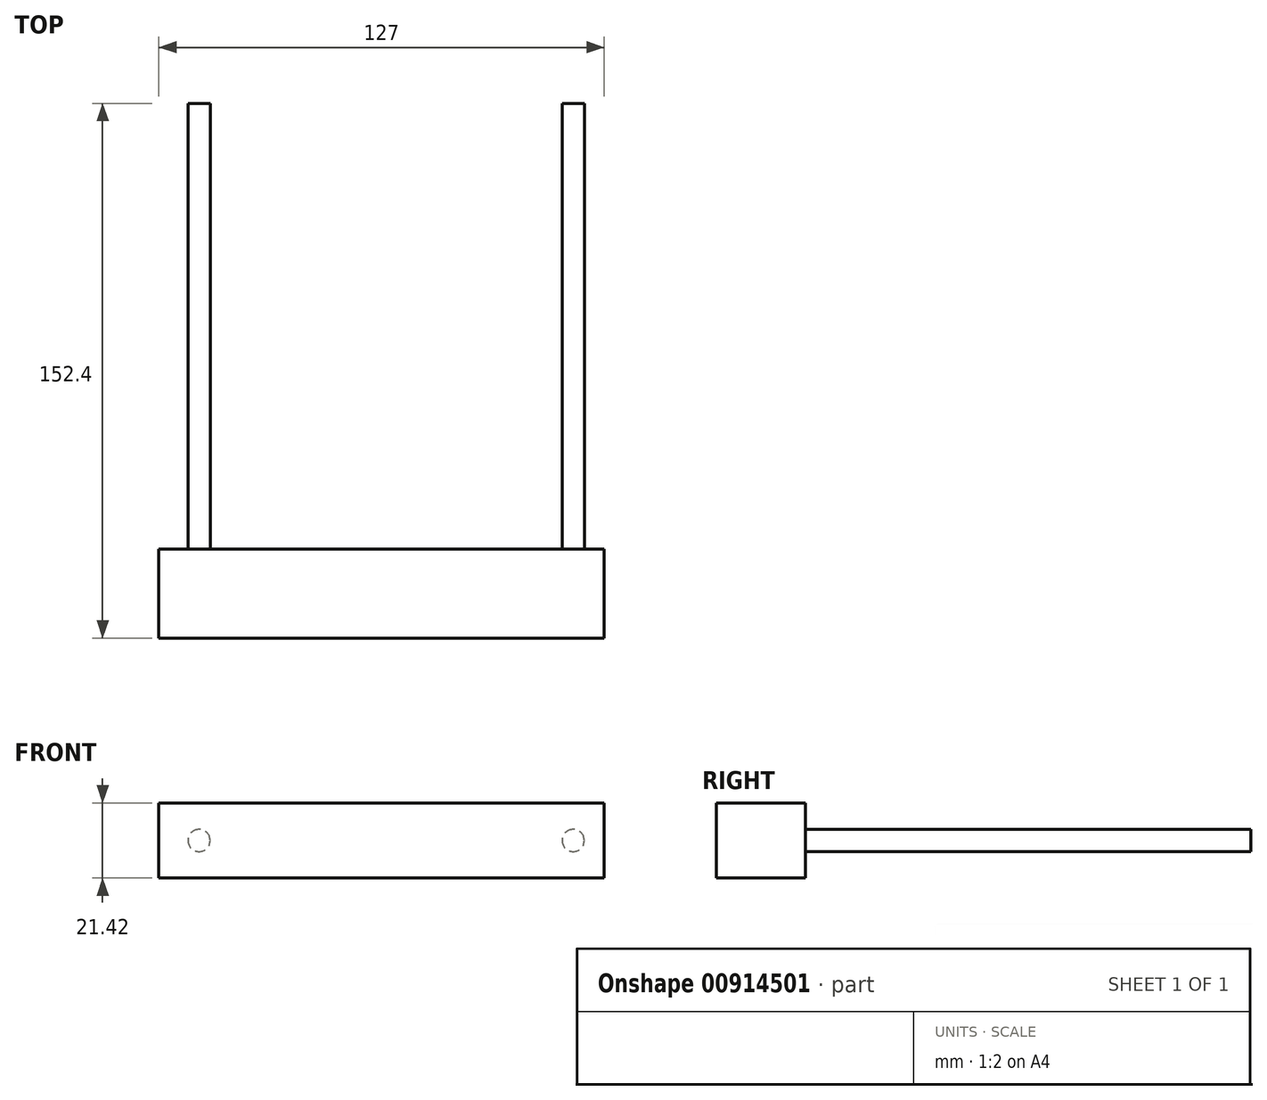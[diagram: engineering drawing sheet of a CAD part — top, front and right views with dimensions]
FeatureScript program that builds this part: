
annotation { "Feature Type Name" : "Feature", "Feature Type Description" : "" }
export const myFeature = defineFeature(function(context is Context, id is Id, definition is map)
    precondition{}
    {
        {
            var Q0;
            Q0=qCreatedBy(makeId("Front.planeOp"),FACE);
            var sketch = newSketch(context, id + "F0", { "sketchPlane" : qUnion([Q0])});
            skLineSegment(sketch, "E0.bottom", {"start": v(63.5, 10.71) * mm, "end": v(-63.5, 10.71) * mm});
            skLineSegment(sketch, "E0.top", {"start": v(63.5, -10.71) * mm, "end": v(-63.5, -10.71) * mm});
            skLineSegment(sketch, "E0.left", {"start": v(63.5, 10.71) * mm, "end": v(63.5, -10.71) * mm});
            skLineSegment(sketch, "E0.right", {"start": v(-63.5, 10.71) * mm, "end": v(-63.5, -10.71) * mm});
            skPoint(sketch, "E0.middle", {"position": v(0, 0) * mm});
            skPoint(sketch, "E1", {"position": v(-52.02, 0) * mm});
            skPoint(sketch, "E2", {"position": v(54.66, 0) * mm});
            skSolve(sketch);
        }
        {
            var Q0;
            Q0 = qSketchRegion(id + "F0", true);
            extrude(context, id + "F1", {"entities" : qUnion([Q0]), "depth" : 25.4 * mm, "offsetDistance" : 25.4 * mm});
        }
        {
            var Q0;
            Q0=makeQuery(id+"F0.imprint","IMPRINT",FACE,{"disambiguationData":[TD([[makeQuery(id+"F0.imprint","IMPRINT",EDGE,{"derivedFrom":sQuery(id+"F0.wireOp",EDGE,"E0.bottom")}),1.0]])]});
            var sketch = newSketch(context, id + "F2", { "sketchPlane" : qUnion([Q0])});
            skCircle(sketch, "E3", {"center": v(54.66, 0) * mm, "radius": 3.18 * mm});
            skCircle(sketch, "E4", {"center": v(-52.02, 0) * mm, "radius": 3.18 * mm});
            skSolve(sketch);
        }
        {
            var Q0;
            Q0 = qSketchRegion(id + "F2", true);
            extrude(context, id + "F3", {"entities" : qUnion([Q0]), "operationType" : NewBodyOperationType.ADD, "oppositeDirection" : true, "depth" : 127 * mm, "offsetDistance" : 25.4 * mm});
        }
    });
